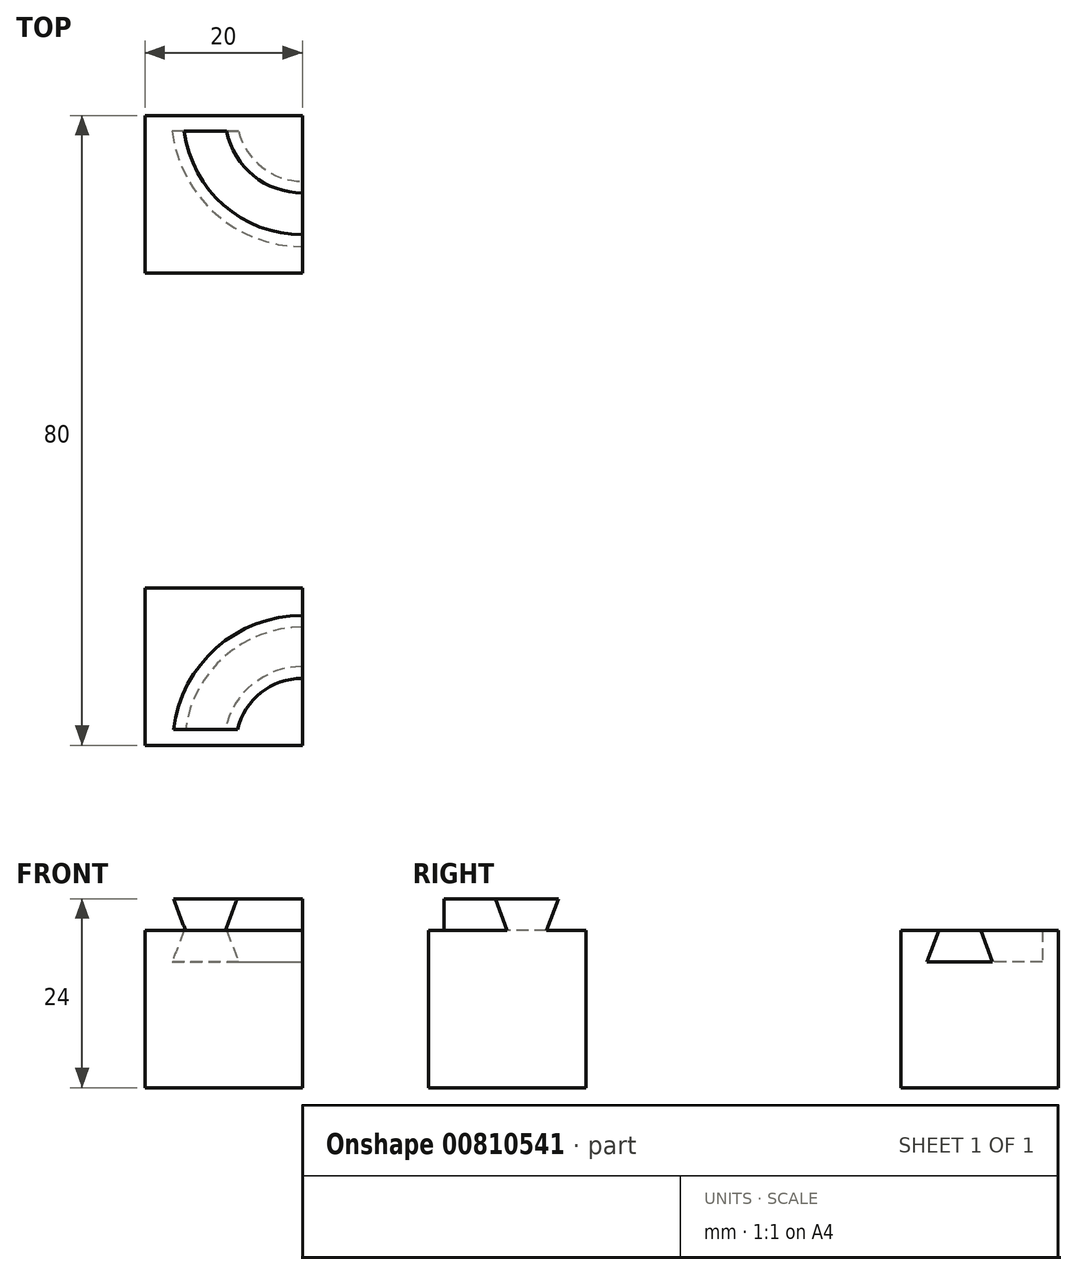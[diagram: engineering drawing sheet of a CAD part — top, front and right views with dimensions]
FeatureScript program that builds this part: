
annotation { "Feature Type Name" : "Feature", "Feature Type Description" : "" }
export const myFeature = defineFeature(function(context is Context, id is Id, definition is map)
    precondition{}
    {
        {
            var Q0;
            Q0=qCreatedBy(makeId("Front.planeOp"),FACE);
            var sketch = newSketch(context, id + "F0", { "sketchPlane" : qUnion([Q0])});
            skLineSegment(sketch, "E0.bottom", {"start": v(10, 10) * mm, "end": v(-10, 10) * mm});
            skLineSegment(sketch, "E0.top", {"start": v(10, -10) * mm, "end": v(-10, -10) * mm});
            skLineSegment(sketch, "E0.left", {"start": v(10, 10) * mm, "end": v(10, -10) * mm});
            skLineSegment(sketch, "E0.right", {"start": v(-10, 10) * mm, "end": v(-10, -10) * mm});
            skPoint(sketch, "E0.middle", {"position": v(0, 0) * mm});
            skSolve(sketch);
        }
        {
            var Q0;
            Q0=makeQuery(id+"F0.imprint","IMPRINT",FACE,{"disambiguationData":[TD([[makeQuery(id+"F0.imprint","IMPRINT",EDGE,{"derivedFrom":sQuery(id+"F0.wireOp",EDGE,"E0.bottom")}),1.0]])]});
            extrude(context, id + "F1", {"entities" : qUnion([Q0]), "depth" : 20 * mm, "offsetDistance" : 25 * mm});
        }
        {
            var Q0;
            Q0=makeQuery(id+"F1.opExtrude","SWEPT_FACE",FACE,{"disambiguationData":[OSD([sQuery(id+"F0.wireOp",EDGE,"E0.bottom")])]});
            var sketch = newSketch(context, id + "F2", { "sketchPlane" : qUnion([Q0])});
            skLineSegment(sketch, "E1.bottom", {"start": v(0, 0) * mm, "end": v(-5, 0) * mm});
            skLineSegment(sketch, "E2", {"start": v(-6.5, 4) * mm, "end": v(1.5, 4) * mm});
            skLineSegment(sketch, "E3", {"start": v(1.5, 4) * mm, "end": v(0, 0) * mm});
            skLineSegment(sketch, "E4", {"start": v(-6.5, 4) * mm, "end": v(-5, 0) * mm});
            skSolve(sketch);
        }
        {
            var Q0;
            Q0=makeQuery(id+"F2.imprint","IMPRINT",FACE,{"disambiguationData":[TD([[makeQuery(id+"F2.imprint","IMPRINT",EDGE,{"derivedFrom":sQuery(id+"F2.wireOp",EDGE,"E1.bottom")}),-1.0]])]});
            var Q1;
            Q1=makeQuery(id+"F1.opExtrude","SWEPT_EDGE",EDGE,{"disambiguationData":[OSD([sQuery(id+"F0.wireOp",EDGE,"E0.bottom"),sQuery(id+"F0.wireOp",EDGE,"E0.left")])]});
            revolve(context, id + "F3", {"operationType" : NewBodyOperationType.ADD, "surfaceOperationType" : NewSurfaceOperationType.NEW, "entities" : qUnion([Q0]), "axis" : qUnion([Q1]), "revolveType" : RevolveType.ONE_DIRECTION, "oppositeDirection" : true, "angle" : 90 * degree});
        }
        {
            var Q0;
            Q0=qCreatedBy(makeId("Front.planeOp"),FACE);
            var sketch = newSketch(context, id + "F4", { "sketchPlane" : qUnion([Q0])});
            skPoint(sketch, "E5.middle", {"position": v(0, 0) * mm});
            skLineSegment(sketch, "E6.bottom", {"start": v(10, 10) * mm, "end": v(-10, 10) * mm});
            skLineSegment(sketch, "E6.top", {"start": v(10, -10) * mm, "end": v(-10, -10) * mm});
            skLineSegment(sketch, "E6.left", {"start": v(10, 10) * mm, "end": v(10, -10) * mm});
            skLineSegment(sketch, "E6.right", {"start": v(-10, 10) * mm, "end": v(-10, -10) * mm});
            skSolve(sketch);
        }
        {
            var Q0;
            Q0=makeQuery(id+"F3.boolean.opBoolean","MERGE",FACE,{"derivedFrom":[makeQuery(id+"F1.opExtrude","SWEPT_FACE",FACE,{"disambiguationData":[OSD([sQuery(id+"F0.wireOp",EDGE,"E0.bottom")])]}),makeQuery(id+"F3.opRevolve","CAP_FACE",FACE,{"disambiguationData":[OSD([sQuery(id+"F2.wireOp",EDGE,"E1.bottom"),sQuery(id+"F2.wireOp",EDGE,"E2"),sQuery(id+"F2.wireOp",EDGE,"E3"),sQuery(id+"F2.wireOp",EDGE,"E4")])],"isStart":true})]});
            var sketch = newSketch(context, id + "F5", { "sketchPlane" : qUnion([Q0])});
            skLineSegment(sketch, "E7.1", {"start": v(-7.75, 6) * mm, "end": v(6.02, 6) * mm});
            skLineSegment(sketch, "E8", {"start": v(6.02, 6) * mm, "end": v(6.02, 0) * mm});
            skLineSegment(sketch, "E9", {"start": v(6.02, 0) * mm, "end": v(-7.75, 0) * mm});
            skLineSegment(sketch, "E10", {"start": v(-7.75, 0) * mm, "end": v(-7.75, 6) * mm});
            skSolve(sketch);
        }
        {
            var Q0;
            Q0 = qSketchRegion(id + "F5", true);
            extrude(context, id + "F6", {"entities" : qUnion([Q0]), "operationType" : NewBodyOperationType.REMOVE, "oppositeDirection" : true, "depth" : 2 * mm, "offsetDistance" : 25 * mm});
        }
        {
            var Q0;
            Q0=qSketchRegion(id+"F4",true);
            extrude(context, id + "F7", {"entities" : qUnion([Q0]), "oppositeDirection" : true, "depth" : 20 * mm, "offsetDistance" : 25 * mm});
        }
        {
            var Q0;
            Q0=makeQuery(id+"F1.opExtrude","SWEPT_BODY",BODY,{"disambiguationData":[OSD([sQuery(id+"F0.wireOp",EDGE,"E0.bottom"),sQuery(id+"F0.wireOp",EDGE,"E0.top"),sQuery(id+"F0.wireOp",EDGE,"E0.left"),sQuery(id+"F0.wireOp",EDGE,"E0.right")])]});
            var Q1;
            Q1=makeQuery(id+"F7.opExtrude","SWEPT_BODY",BODY,{"disambiguationData":[OSD([sQuery(id+"F4.wireOp",EDGE,"E6.bottom"),sQuery(id+"F4.wireOp",EDGE,"E6.top"),sQuery(id+"F4.wireOp",EDGE,"E6.left"),sQuery(id+"F4.wireOp",EDGE,"E6.right")])]});
            var Q2;
            Q2=makeQuery(id+"F3.opRevolve","SWEPT_FACE",FACE,{"disambiguationData":[OSD([sQuery(id+"F2.wireOp",EDGE,"E3")])]});
            var Q3;
            Q3=makeQuery(id+"F3.opRevolve","SWEPT_FACE",FACE,{"disambiguationData":[OSD([sQuery(id+"F2.wireOp",EDGE,"E4")])]});
            booleanBodies(context, id + "F8", {"operationType" : BooleanOperationType.SUBTRACTION, "tools" : qUnion([Q0]), "targets" : qUnion([Q1]), "offset" : true, "entitiesToOffset" : qUnion([Q2, Q3]), "offsetDistance" : 0.15 * mm, "keepTools" : true});
        }
        {
            var Q0;
            Q0=makeQuery(id+"F7.opExtrude","SWEPT_BODY",BODY,{"disambiguationData":[OSD([sQuery(id+"F4.wireOp",EDGE,"E6.bottom"),sQuery(id+"F4.wireOp",EDGE,"E6.top"),sQuery(id+"F4.wireOp",EDGE,"E6.left"),sQuery(id+"F4.wireOp",EDGE,"E6.right")])]});
            var Q1;
            Q1=makeQuery(id+"F7.opExtrude","CAP_EDGE",EDGE,{"disambiguationData":[OSD([sQuery(id+"F4.wireOp",EDGE,"E6.top")])],"isStart":false});
            transform(context, id + "F9", {"entities" : qUnion([Q0]), "transformType" : TransformType.ROTATION, "transformAxis" : qUnion([Q1]), "angle" : 90 * degree, "makeCopy" : false});
        }
        {
            var Q0;
            Q0=makeQuery(id+"F1.opExtrude","SWEPT_BODY",BODY,{"disambiguationData":[OSD([sQuery(id+"F0.wireOp",EDGE,"E0.bottom"),sQuery(id+"F0.wireOp",EDGE,"E0.top"),sQuery(id+"F0.wireOp",EDGE,"E0.left"),sQuery(id+"F0.wireOp",EDGE,"E0.right")])]});
            var Q1;
            Q1=makeQuery(id+"F1.opExtrude","CAP_EDGE",EDGE,{"disambiguationData":[OSD([sQuery(id+"F0.wireOp",EDGE,"E0.top")])],"isStart":false});
            transform(context, id + "F10", {"entities" : qUnion([Q0]), "transformType" : TransformType.ROTATION, "transformAxis" : qUnion([Q1]), "angle" : 90 * degree, "oppositeDirection" : true, "makeCopy" : false});
        }
    });
